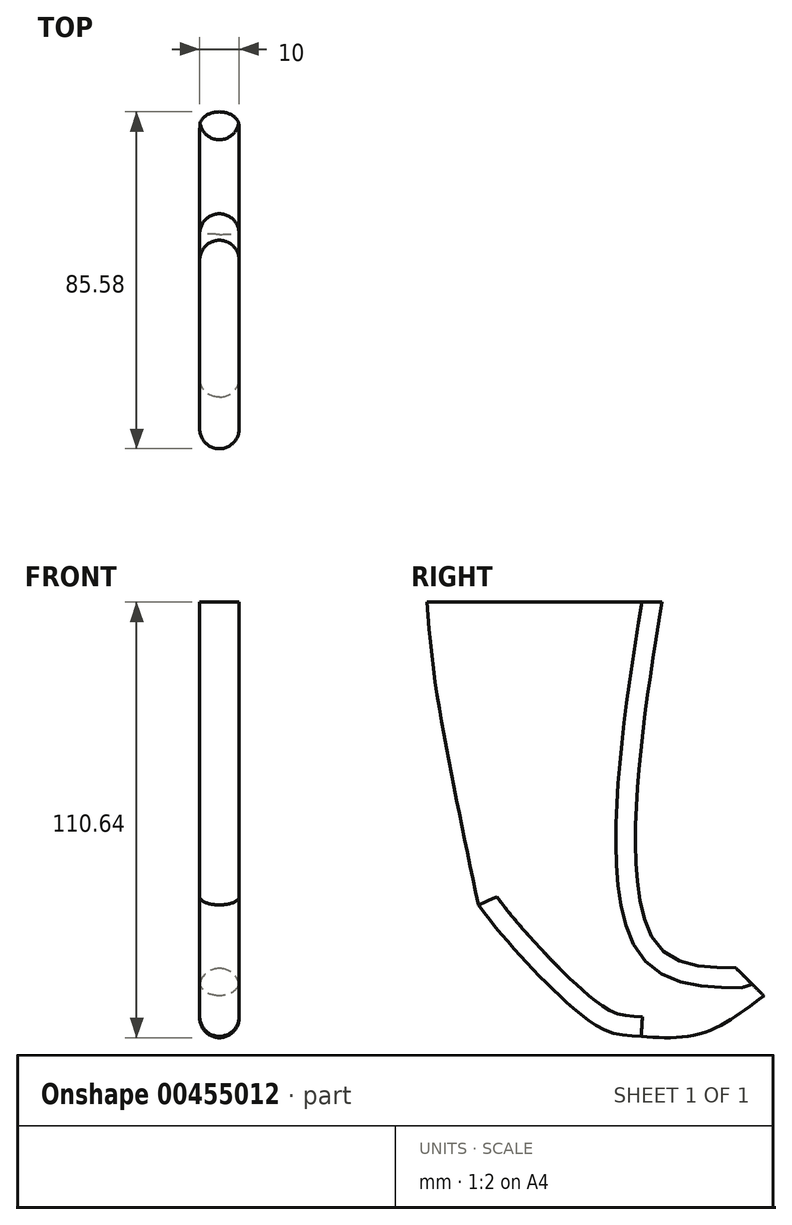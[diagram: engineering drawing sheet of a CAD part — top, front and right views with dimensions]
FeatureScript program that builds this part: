
annotation { "Feature Type Name" : "Feature", "Feature Type Description" : "" }
export const myFeature = defineFeature(function(context is Context, id is Id, definition is map)
    precondition{}
    {
        {
            var Q0;
            Q0=qCreatedBy(makeId("Top.planeOp"),FACE);
            var sketch = newSketch(context, id + "F0", { "sketchPlane" : qUnion([Q0])});
            skLineSegment(sketch, "E0.bottom", {"start": v(50, 50) * mm, "end": v(-50, 50) * mm});
            skLineSegment(sketch, "E0.top", {"start": v(50, -50) * mm, "end": v(-50, -50) * mm});
            skLineSegment(sketch, "E0.left", {"start": v(50, 50) * mm, "end": v(50, -50) * mm});
            skLineSegment(sketch, "E0.right", {"start": v(-50, 50) * mm, "end": v(-50, -50) * mm});
            skPoint(sketch, "E0.middle", {"position": v(0, 0) * mm});
            skSolve(sketch);
        }
        {
            var Q0;
            Q0=qCreatedBy(makeId("Right.planeOp"),FACE);
            var sketch = newSketch(context, id + "F1", { "sketchPlane" : qUnion([Q0])});
            skLineSegment(sketch, "E1", {"start": v(32.93, -92.93) * mm, "end": v(40, -100) * mm});
            skLineSegment(sketch, "E2", {"start": v(40, -100) * mm, "end": v(50, -100) * mm});
            skLineSegment(sketch, "E3", {"start": v(50, -100) * mm, "end": v(50, 0) * mm});
            skFitSpline(sketch, "E4", {"points": [v(14.13, 0) * mm, v(12.54, -86.5) * mm, v(32.93, -92.93) * mm], "startDerivative": vector(-27.8, -165.73) * mm, "endDerivative": vector(72.46, -1.08) * mm});
            skFitSpline(sketch, "E5", {"points": [v(40, -100) * mm, v(24.25, -109.54) * mm, v(8.88, -110.32) * mm], "startDerivative": vector(-29.62, -22.6) * mm, "endDerivative": vector(-32.67, 2.35) * mm});
            skFitSpline(sketch, "E6", {"points": [v(8.88, -110.32) * mm, v(-4.66, -106.18) * mm, v(-32.48, -76.93) * mm], "startDerivative": vector(-48.94, 2.12) * mm, "endDerivative": vector(-28.9, 40.88) * mm});
            skFitSpline(sketch, "E7", {"points": [v(-32.48, -76.93) * mm, v(-43.12, -22.64) * mm, v(-45.58, 0) * mm], "startDerivative": vector(-20.86, 98.62) * mm, "endDerivative": vector(-4.12, 51.82) * mm});
            skLineSegment(sketch, "E8", {"start": v(14.13, 0) * mm, "end": v(-45.58, 0) * mm});
            skSolve(sketch);
        }
        {
            var Q0;
            Q0=makeQuery(id+"F1.imprint","IMPRINT",FACE,{"disambiguationData":[TD([[makeQuery(id+"F1.imprint","IMPRINT",EDGE,{"derivedFrom":sQuery(id+"F1.wireOp",EDGE,"E1")}),-1.0]])]});
            extrude(context, id + "F2", {"entities" : qUnion([Q0]), "endBound" : BoundingType.SYMMETRIC, "depth" : 10 * mm});
        }
        {
            var Q0;
            Q0=makeQuery(id+"F2.opExtrude","CAP_EDGE",EDGE,{"disambiguationData":[OSD([sQuery(id+"F1.wireOp",EDGE,"E4")])],"isStart":false});
            var Q1;
            Q1=makeQuery(id+"F2.opExtrude","CAP_EDGE",EDGE,{"disambiguationData":[OSD([sQuery(id+"F1.wireOp",EDGE,"E5")])],"isStart":false});
            var Q2;
            Q2=makeQuery(id+"F2.opExtrude","CAP_EDGE",EDGE,{"disambiguationData":[OSD([sQuery(id+"F1.wireOp",EDGE,"E6")])],"isStart":false});
            var Q3;
            Q3=makeQuery(id+"F2.opExtrude","CAP_EDGE",EDGE,{"disambiguationData":[OSD([sQuery(id+"F1.wireOp",EDGE,"E7")])],"isStart":false});
            var Q4;
            Q4=makeQuery(id+"F2.opExtrude","CAP_EDGE",EDGE,{"disambiguationData":[OSD([sQuery(id+"F1.wireOp",EDGE,"E4")])],"isStart":true});
            var Q5;
            Q5=makeQuery(id+"F2.opExtrude","CAP_EDGE",EDGE,{"disambiguationData":[OSD([sQuery(id+"F1.wireOp",EDGE,"E7")])],"isStart":true});
            var Q6;
            Q6=makeQuery(id+"F2.opExtrude","CAP_EDGE",EDGE,{"disambiguationData":[OSD([sQuery(id+"F1.wireOp",EDGE,"E6")])],"isStart":true});
            fillet(context, id + "F3", {"entities" : qUnion([Q0, Q1, Q2, Q3, Q4, Q5, Q6]), "radius" : 5 * mm, "tangentPropagation" : true, "allowEdgeOverflow" : false});
        }
    });
